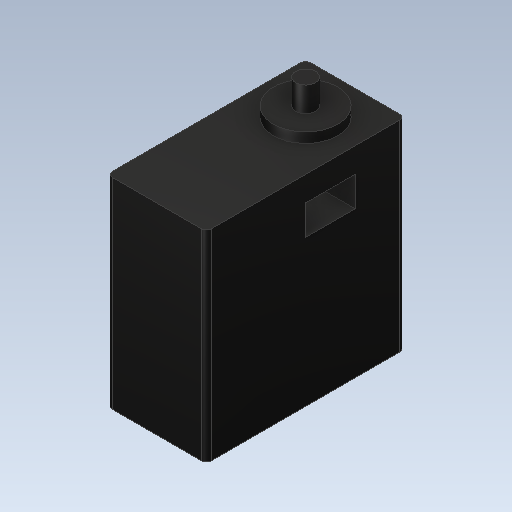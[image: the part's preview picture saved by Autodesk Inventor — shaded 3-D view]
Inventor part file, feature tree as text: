
AUTODESK INVENTOR PART (.ipt)
format: ipt  version: 2020.1 (Build 241239000, 239)  size: 157,696 bytes
history: native  units: mm
features: extrude x8, sketch x8, fillet x1
ambient origin geometry x8: Origin, YZ Plane, XZ Plane, XY Plane, X Axis, Y Axis, Z Axis, Center Point
bodies: Solid1 (feature_tree)
feature tree (17):
  extrude  "Extrusion1"  Depth=20.0mm
  extrude  "Extrusion2"  Depth=10.0mm
  extrude  "Extrusion3"  Depth=1.0mm TaperAngle=0.0deg
  fillet  "Fillet1"  Radius=4.0mm
  extrude  "Extrusion4"  Depth=1.0mm
  extrude  "Extrusion5"  Depth=10.0mm
  extrude  "Extrusión6"  Depth=1.0mm
  extrude  "Extrusión8"  Depth=5.0mm
  extrude  "Extrusión9"  Depth=6.0mm
  sketch  "Sketch1"  dims[d0=40.5mm d1=20.0mm]
  sketch  "Sketch2"  dims[d2=40.0mm d3=0.0mm d4=10.0mm]
  sketch  "Sketch3"  dims[d5=10.0mm d6=1.0mm d7=0.0mm d8=4.0mm]
  sketch  "Sketch4"  dims[d9=6.0mm d10=0.0mm d11=1.0mm]
  sketch  "Sketch5"  dims[d12=10.0mm d13=10.0mm]
  sketch  "Boceto6"  dims[d14=1.0mm d15=0.0mm d16=4.0mm]
  sketch  "Boceto7"  dims[d17=4.0mm d18=0.0mm d19=5.0mm]
  sketch  "Boceto8"  dims[d20=10.0mm d21=6.0mm d22=10.0mm d23=10.0mm d24=0.0mm d25=13.0mm d28=2.0mm d29=0.0mm d30=13.0mm d31=2.0mm d32=0.0mm]
